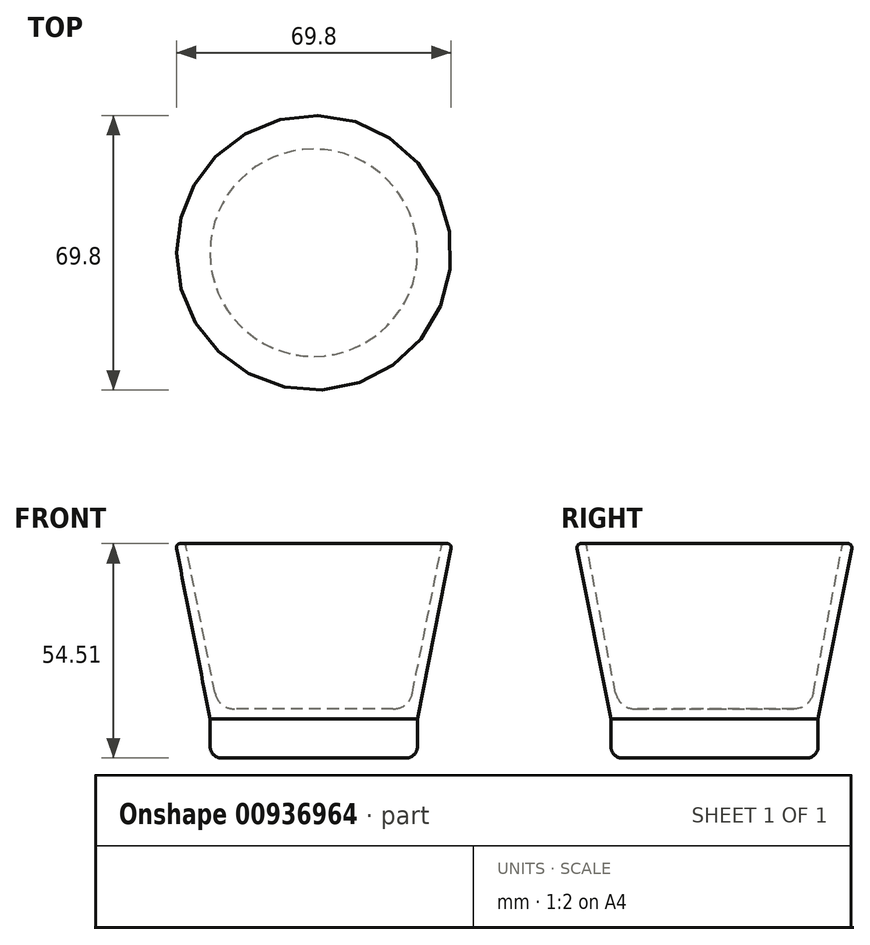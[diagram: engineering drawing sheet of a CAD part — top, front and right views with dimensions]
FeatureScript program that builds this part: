
annotation { "Feature Type Name" : "Feature", "Feature Type Description" : "" }
export const myFeature = defineFeature(function(context is Context, id is Id, definition is map)
    precondition{}
    {
        {
            var Q0;
            Q0=qCreatedBy(makeId("Front.planeOp"),FACE);
            var sketch = newSketch(context, id + "F0", { "sketchPlane" : qUnion([Q0])});
            skLineSegment(sketch, "E0", {"start": v(-35.12, 44.51) * mm, "end": v(-26.34, 0) * mm});
            skLineSegment(sketch, "E1", {"start": v(-26.34, 0) * mm, "end": v(0, 0) * mm});
            skLineSegment(sketch, "E2", {"start": v(0, 0) * mm, "end": v(0, 44.51) * mm});
            skLineSegment(sketch, "E3", {"start": v(0, 44.51) * mm, "end": v(-35.12, 44.51) * mm});
            skSolve(sketch);
        }
        {
            var Q0;
            Q0 = qSketchRegion(id + "F0", true);
            var Q1;
            Q1=sQuery(id+"F0.wireOp",EDGE,"E2");
            revolve(context, id + "F1", {"surfaceOperationType" : NewSurfaceOperationType.NEW, "entities" : qUnion([Q0]), "axis" : qUnion([Q1]), "revolveType" : RevolveType.FULL});
        }
        {
            var Q0;
            Q0=makeQuery(id+"F1.opRevolve","SWEPT_FACE",FACE,{"disambiguationData":[OSD([sQuery(id+"F0.wireOp",EDGE,"E3")])]});
            shell(context, id + "F2", {"entities" : qUnion([Q0]), "thickness" : 2.5 * mm});
        }
        {
            var Q0;
            Q0=makeQuery(id+"F1.opRevolve","SWEPT_FACE",FACE,{"disambiguationData":[OSD([sQuery(id+"F0.wireOp",EDGE,"E1")])]});
            extrude(context, id + "F3", {"entities" : qUnion([Q0]), "operationType" : NewBodyOperationType.ADD, "depth" : 10 * mm, "offsetDistance" : 25 * mm});
        }
        {
            var Q0;
            Q0=makeQuery(id+"F2.opShell","OFFSET_EDGE",EDGE,{"disambiguationData":[OSD([sQuery(id+"F0.wireOp",EDGE,"E0"),sQuery(id+"F0.wireOp",EDGE,"E1")])]});
            fillet(context, id + "F4", {"entities" : qUnion([Q0]), "radius" : 5 * mm, "tangentPropagation" : true, "allowEdgeOverflow" : false});
        }
        {
            var Q0;
            Q0=makeQuery(id+"F2.opShell","OFFSET_EDGE",EDGE,{"disambiguationData":[OSD([sQuery(id+"F0.wireOp",EDGE,"E0"),sQuery(id+"F0.wireOp",EDGE,"E3")])]});
            var Q1;
            Q1=makeQuery(id+"F1.opRevolve","SWEPT_EDGE",EDGE,{"disambiguationData":[OSD([sQuery(id+"F0.wireOp",EDGE,"E0"),sQuery(id+"F0.wireOp",EDGE,"E3")])]});
            fillet(context, id + "F5", {"entities" : qUnion([Q0, Q1]), "radius" : 1 * mm, "tangentPropagation" : true, "allowEdgeOverflow" : false});
        }
        {
            var Q0;
            Q0=makeQuery(id+"F3.opExtrude","CAP_FACE",FACE,{"disambiguationData":[OSD([sQuery(id+"F0.wireOp",EDGE,"E1")])],"isStart":false});
            fillet(context, id + "F6", {"entities" : qUnion([Q0]), "radius" : 3 * mm, "tangentPropagation" : true, "allowEdgeOverflow" : false});
        }
    });
